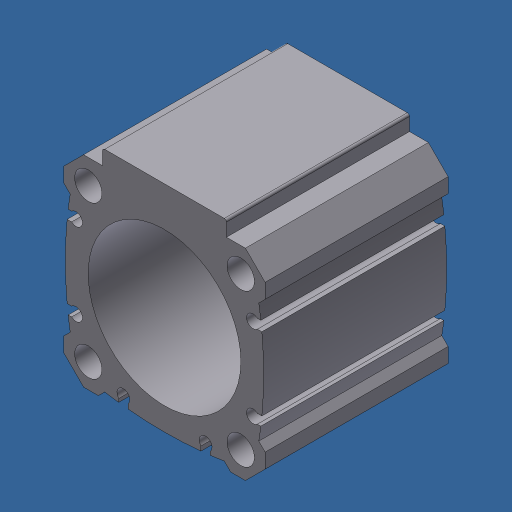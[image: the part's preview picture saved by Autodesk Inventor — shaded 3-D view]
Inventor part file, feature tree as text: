
AUTODESK INVENTOR PART (.ipt)
format: ipt  version: 2024.3 (Build 283343000, 343)  size: 227,328 bytes
history: native  units: mm (DEFAULTED — no unit token found)
features: other x1, extrude x1, hole x1, sketch x1
ambient origin geometry x8: Origin, YZ Plane, XZ Plane, XY Plane, X Axis, Y Axis, Z Axis, Center Point
bodies: Body1 (feature_tree)
feature tree (4):
  other  "Finish - None"
  extrude  "PHD, 50MM"  Depth=50.08mm
  hole  "Hole1"  [1 undecoded]
  sketch  "Sketch1"  dims[d0=4.2418mm d1=50.08mm d2=241.885813mm d3=0.712mm d4=60.0mm d5=0.0mm d6=25.0mm d7=25.0mm d8=25.0mm d9=25.0mm d10=9.0mm d11=6.0mm d12=4.0mm d13=2.0mm d14=14.3117mm d15=8.0mm d16=20.594885mm]
note: 1 required parameter value undecoded (feature->parameter linkage not recoverable at this tier; creation-order binding heuristic only, values carry confidence <= 0.55)
